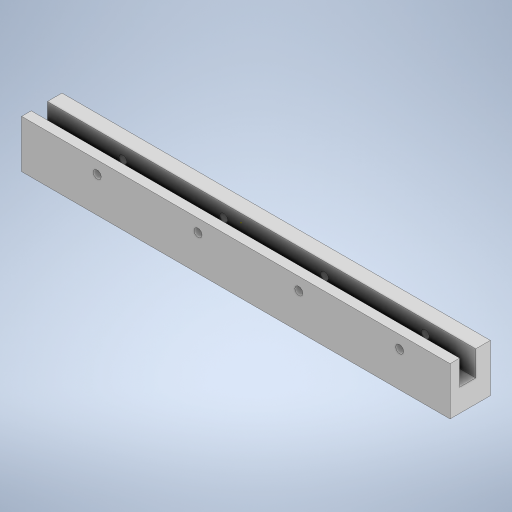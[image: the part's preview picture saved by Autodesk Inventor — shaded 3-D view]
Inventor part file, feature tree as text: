
AUTODESK INVENTOR PART (.ipt)
format: ipt  version: 2023 (Build 270158000, 158)  size: 349,696 bytes
history: native  units: mm
features: sketch x15, extrude x9, hole x5, other x1
ambient origin geometry x8: Origin, YZ Plane, XZ Plane, XY Plane, X Axis, Y Axis, Z Axis, Center Point
bodies: Body1 (feature_tree)
feature tree (30):
  other  "ソリッド1"
  extrude  "押し出し1"  Depth=180.0mm
  extrude  "押し出し2"  Depth=6.0mm
  extrude  "押し出し3"  Depth=17.0mm TaperAngle=0.0deg
  extrude  "押し出し4"  Depth=170.0mm
  extrude  "押し出し5"  Depth=6.0mm
  hole  "穴1"  [1 undecoded]
  hole  "穴2"  [1 undecoded]
  extrude  "押し出し6"  Depth=14.0mm TaperAngle=0.0deg
  hole  "穴3"  [1 undecoded]
  extrude  "押し出し7"  Depth=13.0mm TaperAngle=0.0deg
  extrude  "押し出し8"  Depth=6.4mm
  sketch  "スケッチ13"
  hole  "穴4"  [1 undecoded]
  extrude  "押し出し9"  Depth=5.0mm
  hole  "穴5"  [1 undecoded]
  sketch  "スケッチ1"
  sketch  "スケッチ2"
  sketch  "スケッチ3"
  sketch  "スケッチ4"
  sketch  "スケッチ5"
  sketch  "スケッチ6"
  sketch  "スケッチ7"
  sketch  "スケッチ8"
  sketch  "スケッチ10"
  sketch  "スケッチ11"
  sketch  "スケッチ12"
  sketch  "スケッチ14"
  sketch  "スケッチ15"
  sketch  "スケッチ16"
note: 5 required parameter values undecoded (feature->parameter linkage not recoverable at this tier; creation-order binding heuristic only, values carry confidence <= 0.55)
